# Revit family: VT.VAR30.G.07
name_source: partatom
category: Оборудование
units: mm (PartAtom-declared; Revit-internal decimal feet)

## family parameters
Всегда вертикально = Да
Заголовок OmniClass = Climate Control (HVAC)
На основе рабочей плоскости = Нет
Номер OmniClass = 23.75.00.00
Общий = Нет
При загрузке вырезать с полостями = Нет
Размер круглого соединителя = Использовать диаметр
Тип детали = Нормальный
Точка расчета площади = Нет

## types (1)
- VT.VAR30.G.07
    1.4 Описание = Климат-контроль установки и оборудование (HVAC)
    2.0 Описание = Клапаны
    Article Description = Modular distribution manifold for VARIMIX system
    Article Type = VAR30
    BIMобъект категории = Другие
    BIMобъект основная категория = Водопровод
    Revit Version = 2018
    URL = https://valtec.ru
    Uniclass 2015 Name = Системы отопления, охлаждения и охлаждения
    Вес нетто (кг) = 4.5
    Гидравлический возвратный поток 1 = 0.0 л/с
    Гидравлический поток подачи 1 = 0.0 л/с
    Гидравлический терминал обратного потока = 0.0 л/с
    Гидравлический терминал подачи = 0.0 л/с
    Группа модели = VAR30
    Группа товаров = VARIMIX
    Изготовитель = IVAR
    Инструкция по установке = https://valtec.ru
    Классификация IFC = 5/5000
Клапан
    Код категории BIMобъекта = водопроводным-другой
    Код основной категории BIMobject = водопровод
    Макс рабочая температура (°C) = 120 °C
    Макс рабочее давление (бар) = 10 бары
    Максимальная скорость потока (л/ч) = 4500
    Мастерформат 2014 Описание = Отопление, вентиляция и кондиционирование воздуха (HVAC)
    Материал = Латунь - CB753S
    Материал основной = Латунь
    Номинальная высота = 0 мм
    Номинальная ширина = 0 мм
    Общий поток подачи гидравлики = 0.0 л/с
    Описание = Modular distribution manifold for VARIMIX system
    Описание Конфигурации = Модульный распределительный коллектор для системы VARIMIX
    Пенополистрирольная теплоизоляция = Да
    Полный гидравлический возвратный поток = 0.0 л/с
    Продукта url = https://valtec.ru
    Произведено в = Made in Italy
    Размер соединения = G 1"1/4
    Страна изготовитель = Italy
    Техническое описание = https://valtec.ru
